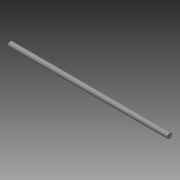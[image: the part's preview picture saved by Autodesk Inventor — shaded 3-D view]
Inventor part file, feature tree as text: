
AUTODESK INVENTOR PART (.ipt)
format: ipt  version: 2013 (Build 170138000, 138)  size: 64,512 bytes
history: native  units: in
note: dims shown in document units (in); Inventor stores cm internally (conversion verified against a paired STEP export)
features: sketch x2, sweep x1
ambient origin geometry x8: Origin, YZ Plane, XZ Plane, XY Plane, X Axis, Y Axis, Z Axis, Center Point
bodies: Solid1 (feature_tree)
feature tree (3):
  sweep  "Sweep1"
  sketch  "Sketch1"  dims[d0=16.0in d1=0.5in]
  sketch  "Sketch2"  dims[d2=0.0in]
